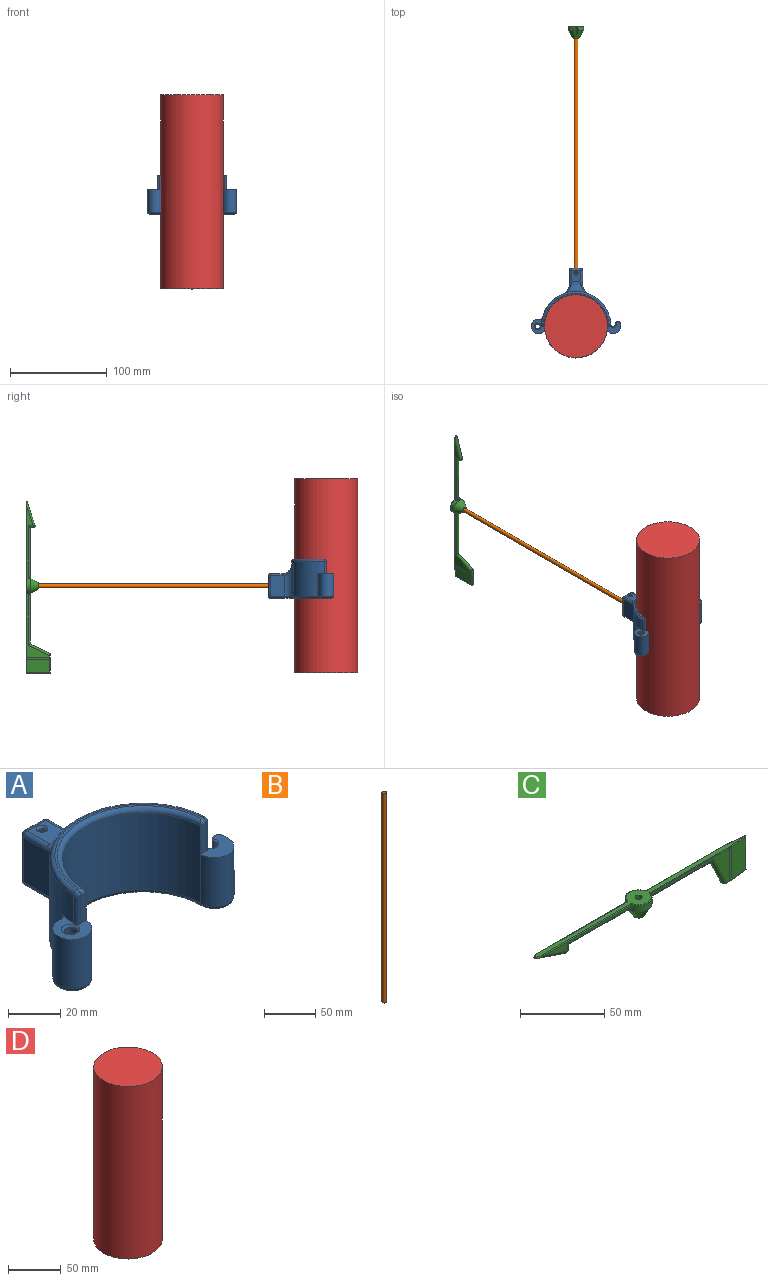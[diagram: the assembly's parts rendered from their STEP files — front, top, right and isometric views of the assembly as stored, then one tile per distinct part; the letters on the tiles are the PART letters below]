
ASSEMBLY  parts=4 mates=3
PART A: 71 faces, bbox 93.2x68.2x42.1 mm
  f0: cylinder r=2mm len=19mm, axis (0,1,0), area 228.4mm2, adj f22,f26,f27,f68
  f1: plane 13x2.94mm, normal (0,-1,0), area 38.2mm2, adj f4,f16,f63,f66
  f2: cylinder r=36mm len=71.88mm, axis (0,0,-1), area 2847.7mm2, adj f7,f17,f20,f23,f24,f25,f36,f39
  f3: plane 13x2.94mm, normal (0,-1,0), area 38.2mm2, adj f4,f7,f59,f60
  f4: cylinder r=31mm len=62mm, axis (0,0,-1), area 3506mm2, adj f1,f3,f8,f9,f33,f61
  f5: plane 67.88x32mm, normal (0,0,1), area 101.2mm2, adj f59,f61,f63,f64
  f6: plane 12.27x10mm, normal (0,0,1), area 105mm2, adj f24,f49,f53,f55,f67
  f7: plane 16.77x15mm, normal (0,0,1), area 116.2mm2, adj f2,f3,f9,f20,f60,f69
  f8: cylinder r=7.5mm len=23mm, axis (0,0,1), area 541.9mm2, adj f4,f14,f16,f31
  f9: cylinder r=7.5mm len=23mm, axis (0,0,1), area 835.4mm2, adj f4,f7,f20,f35
  f10: plane 21.38x15.26mm, normal (-1,0,0), area 320.8mm2, adj f25,f46,f52,f55,f56
  f11: plane 21x10mm, normal (0,1,0), area 181.7mm2, adj f47,f48,f52,f53,f68
  f12: plane 21.38x15.26mm, normal (1,0,0), area 320.8mm2, adj f23,f40,f45,f48,f49
  f13: plane 22.05x0.08mm, normal (0,1,0), area 1.8mm2, adj f17,f19,f32,f70
  f14: plane 23x2.5mm, normal (1,0,0), area 57.5mm2, adj f8,f16,f18,f29
  f15: plane 88x63.5mm, normal (0,0,-1), area 418.6mm2, adj f28,f29,f30,f31,f32,f33,f34,f35
  f16: plane 15x12.5mm, normal (0,0,1), area 105mm2, adj f1,f8,f14,f18,f66,f70
  f17: cylinder r=2.5mm len=22.39mm, axis (0,0,-1), area 84mm2, adj f2,f13,f34,f70
  f18: cylinder r=2.5mm len=23mm, axis (0,0,1), area 180mm2, adj f14,f16,f19,f28,f70
  f19: cylinder r=2.5mm len=22mm, axis (0,0,-1), area 86.4mm2, adj f13,f18,f30,f70
  f20: cylinder r=2.5mm len=23mm, axis (0,0,-1), area 82.8mm2, adj f2,f7,f9,f37
  f21: cylinder r=2.5mm len=22mm, axis (0,0,1), area 345.6mm2, adj f58,f69
  f22: cone r=0mm half-angle=59deg, axis (0,1,0), area 14.7mm2, adj f0
  f23: cylinder r=10mm len=33mm, axis (0,0,-1), area 310.3mm2, adj f2,f12,f38,f41
  f24: torus R=46mm, axis (0,0,-1), area 240.9mm2, adj f2,f6,f41,f45,f56,f57
  f25: cylinder r=10mm len=33mm, axis (0,0,-1), area 310.3mm2, adj f2,f10,f42,f57
  f26: cylinder r=1.25mm len=8.94mm, axis (0,0,1), area 68.4mm2, adj f0,f43
  f27: cylinder r=1.25mm len=9.94mm, axis (0,0,1), area 76.3mm2, adj f0,f67
  f28: torus R=0.5mm, axis (0,0,-1), area 17.5mm2, adj f15,f18,f29,f30
  f29: cylinder r=2mm len=2.5mm, axis (0,1,0), area 7.9mm2, adj f14,f15,f28,f31
  f30: torus R=4.5mm, axis (0,0,-1), area 15.9mm2, adj f15,f19,f28,f32
  f31: torus R=5.5mm, axis (0,0,-1), area 66.8mm2, adj f8,f15,f29,f33
  f32: cylinder r=2mm len=2mm, axis (-1,0,0), area 0.3mm2, adj f13,f15,f30,f34
  f33: torus R=33mm, axis (0,0,-1), area 313.1mm2, adj f4,f15,f31,f35
  f34: torus R=4.5mm, axis (0,0,-1), area 15.3mm2, adj f15,f17,f32,f36
  f35: torus R=5.5mm, axis (0,0,-1), area 103mm2, adj f9,f15,f33,f37
  f36: torus R=34mm, axis (0,0,-1), area 124.9mm2, adj f2,f15,f34,f38
  f37: torus R=4.5mm, axis (0,0,-1), area 14.6mm2, adj f15,f20,f35,f39
  f38: torus R=12mm, axis (0,0,-1), area 40.2mm2, adj f15,f23,f36,f40
  f39: torus R=34mm, axis (0,0,-1), area 103.3mm2, adj f2,f15,f37,f42
  f40: cylinder r=2mm len=15.26mm, axis (0,1,0), area 47.9mm2, adj f12,f15,f38,f44
  f41: bspline ~11.97x11.41mm, area 27.7mm2, adj f23,f24,f45
  f42: torus R=12mm, axis (0,0,-1), area 40.2mm2, adj f15,f25,f39,f46
  f43: torus R=3.25mm, axis (0,0,-1), area 38.8mm2, adj f15,f26,f47
  f44: sphere r=2mm, area 6.3mm2, adj f40,f47,f48
  f45: bspline ~5.65x2.65mm, area 8.4mm2, adj f12,f24,f41,f49
  f46: cylinder r=2mm len=15.26mm, axis (0,-1,0), area 47.9mm2, adj f10,f15,f42,f50
  f47: cylinder r=2mm len=10mm, axis (-1,0,0), area 31.2mm2, adj f11,f15,f43,f44,f50
  f48: cylinder r=2mm len=21mm, axis (0,0,1), area 66mm2, adj f11,f12,f44,f51
  f49: cylinder r=2mm len=12.27mm, axis (0,-1,0), area 38.6mm2, adj f6,f12,f45,f51
  f50: sphere r=2mm, area 6.3mm2, adj f46,f47,f52
  f51: sphere r=2mm, area 6.3mm2, adj f48,f49,f53
  f52: cylinder r=2mm len=21mm, axis (0,0,1), area 66mm2, adj f10,f11,f50,f54
  f53: cylinder r=2mm len=10mm, axis (1,0,0), area 31.4mm2, adj f6,f11,f51,f54
  f54: sphere r=2mm, area 6.3mm2, adj f52,f53,f55
  f55: cylinder r=2mm len=12.27mm, axis (0,1,0), area 38.6mm2, adj f6,f10,f54,f56
  f56: bspline ~5.65x2.65mm, area 8.4mm2, adj f10,f24,f55,f57
  f57: bspline ~11.97x11.41mm, area 27.7mm2, adj f24,f25,f56
  f58: torus R=4.5mm, axis (0,0,-1), area 63.7mm2, adj f15,f21
  f59: cylinder r=2mm len=2.94mm, axis (-1,0,0), area 7mm2, adj f3,f5,f61,f62
  f60: cylinder r=2mm len=13mm, axis (0,0,-1), area 42.4mm2, adj f2,f3,f7,f62
  f61: torus R=33mm, axis (0,0,1), area 308.6mm2, adj f4,f5,f59,f63
  f62: sphere r=2mm, area 6.5mm2, adj f59,f60,f64
  f63: cylinder r=2mm len=2.94mm, axis (-1,0,0), area 7mm2, adj f1,f5,f61,f65
  f64: torus R=34mm, axis (0,0,1), area 335.1mm2, adj f2,f5,f62,f65
  f65: sphere r=2mm, area 6.5mm2, adj f63,f64,f66
  f66: cylinder r=2mm len=13.58mm, axis (0,0,-1), area 42.7mm2, adj f1,f2,f16,f65,f70
  f67: torus R=2.25mm, axis (0,0,-1), area 15.9mm2, adj f6,f27
  f68: torus R=3mm, axis (0,-1,0), area 23.3mm2, adj f0,f11
  f69: torus R=3.5mm, axis (0,0,-1), area 28.3mm2, adj f7,f21
  f70: torus R=3.5mm, axis (0,0,-1), area 12.9mm2, adj f2,f13,f16,f17,f18,f19,f66
PART B: 3 faces, bbox 4x4x250 mm
  f0: cylinder r=2mm len=250mm, axis (0,0,-1), area 3141.6mm2, adj f1,f2
  f1: plane 4x4mm, normal (0,0,1), area 12.6mm2, adj f0
  f2: plane 4x4mm, normal (0,0,-1), area 12.6mm2, adj f0
PART C: 56 faces, bbox 177.5x17.3x26.3 mm
  f0: plane 65.88x24mm, normal (0,-1,0), area 264.9mm2, adj f3,f11,f12,f18,f26,f49
  f1: plane 65.88x24mm, normal (0,1,0), area 264.9mm2, adj f11,f12,f19,f25,f36,f53
  f2: cylinder r=2mm len=53.88mm, axis (-1,0,0), area 327.3mm2, adj f8,f9,f39,f46
  f3: cylinder r=0.5mm len=65.88mm, axis (1,0,0), area 51.7mm2, adj f0,f5,f24,f47
  f4: cylinder r=0.5mm len=74.05mm, axis (-1,0,0), area 58.2mm2, adj f5,f9,f22,f50
  f5: plane 176.89x15mm, normal (0,0,1), area 623.7mm2, adj f3,f4,f21,f22,f24,f25,f27,f28
  f6: plane 18.71x3mm, normal (0,0,-1), area 33.5mm2, adj f10,f23,f26,f29,f32,f34,f35,f36
  f7: plane 25x0.1mm, normal (1,0,0), area 2.4mm2, adj f27,f30,f31,f32,f33,f34
  f8: plane 74.05x6.73mm, normal (0,-1,0), area 148.7mm2, adj f2,f13,f14,f21,f44
  f9: plane 74.05x6.73mm, normal (0,1,0), area 148.7mm2, adj f2,f4,f13,f14,f48
  f10: cylinder r=2mm len=2.71mm, axis (0,1,0), area 3.4mm2, adj f6,f20,f38
  f11: cylinder r=2mm len=23.36mm, axis (-0.43,0,0.9), area 147.2mm2, adj f0,f1,f12,f20,f23,f37,f38
  f12: cylinder r=2mm len=53.14mm, axis (-1,0,0), area 327.6mm2, adj f0,f1,f11,f51
  f13: cylinder r=2mm len=25.09mm, axis (-0.95,0,0.32), area 151.6mm2, adj f8,f9,f15,f22
  f14: cylinder r=2mm len=5.23mm, axis (0,0,-1), area 22.8mm2, adj f8,f9,f15,f39
  f15: sphere r=2mm, area 15.1mm2, adj f13,f14
  f16: plane 24x13.56mm, normal (0.1,1,0), area 327mm2, adj f19,f31,f33,f34
  f17: plane 24x13.56mm, normal (0.1,-1,0), area 327mm2, adj f18,f27,f30,f32
  f18: cylinder r=20mm len=24mm, axis (0,0,-1), area 47.8mm2, adj f0,f17,f24,f29
  f19: cylinder r=20mm len=24mm, axis (0,0,1), area 47.8mm2, adj f1,f16,f28,f35
  f20: bspline ~1.97x1.87mm, area 1mm2, adj f10,f11,f23
  f21: cylinder r=0.5mm len=74.05mm, axis (1,0,0), area 58.2mm2, adj f5,f8,f22,f43
  f22: bspline ~5.23x4mm, area 12.7mm2, adj f4,f5,f13,f21
  f23: bspline ~1.51x0.75mm, area 0.6mm2, adj f6,f11,f20,f26
  f24: torus R=19.5mm, axis (0,0,1), area 1.6mm2, adj f3,f5,f18,f27
  f25: cylinder r=0.5mm len=65.88mm, axis (-1,0,0), area 51.7mm2, adj f1,f5,f28,f54
  f26: cylinder r=0.5mm len=2.03mm, axis (-1,0,0), area 1.6mm2, adj f0,f6,f23,f29
  f27: cylinder r=0.5mm len=14.11mm, axis (-1,-0.1,0), area 11mm2, adj f5,f7,f17,f24,f30,f31
  f28: torus R=19.5mm, axis (0,0,1), area 1.6mm2, adj f5,f19,f25,f31
  f29: torus R=19.5mm, axis (0,0,-1), area 1.6mm2, adj f6,f18,f26,f32
  f30: cylinder r=0.5mm len=25mm, axis (0,0,1), area 18.1mm2, adj f7,f17,f27,f32
  f31: cylinder r=0.5mm len=14.11mm, axis (-1,0.1,0), area 11mm2, adj f5,f7,f16,f27,f28,f33
  f32: cylinder r=0.5mm len=14.11mm, axis (1,0.1,0), area 11mm2, adj f6,f7,f17,f29,f30,f34
  f33: cylinder r=0.5mm len=25mm, axis (0,0,1), area 18.1mm2, adj f7,f16,f31,f34
  f34: cylinder r=0.5mm len=14.11mm, axis (1,-0.1,0), area 11mm2, adj f6,f7,f16,f32,f33,f35
  f35: torus R=19.5mm, axis (0,0,-1), area 1.6mm2, adj f6,f19,f34,f36
  f36: cylinder r=0.5mm len=2.03mm, axis (1,0,0), area 1.6mm2, adj f1,f6,f35,f37
  f37: bspline ~1.51x0.75mm, area 0.6mm2, adj f6,f11,f36,f38
  f38: bspline ~1.97x1.87mm, area 1mm2, adj f10,f11,f37
  f39: bspline ~4x2.5mm, area 3.5mm2, adj f2,f14
  f40: cylinder r=8mm len=16mm, axis (0,0,1), area 193.2mm2, adj f41,f44,f45,f46,f48,f49,f51,f52
  f41: cone r=8mm half-angle=31.8deg, axis (0,0,1), area 326.5mm2, adj f40,f42
  f42: plane 6.08x6.08mm, normal (0,0,-1), area 15.2mm2, adj f41,f55
  f43: torus R=1mm, axis (0,0,1), area 0.7mm2, adj f5,f21,f44,f45
  f44: cylinder r=0.5mm len=1.5mm, axis (0,0,1), area 1mm2, adj f8,f40,f43,f46
  f45: torus R=7.5mm, axis (0,0,1), area 15.6mm2, adj f5,f40,f43,f47
  f46: bspline ~4.71x3.05mm, area 4.8mm2, adj f2,f40,f44,f48
  f47: torus R=1mm, axis (0,0,1), area 0.7mm2, adj f3,f5,f45,f49
  f48: cylinder r=0.5mm len=1.5mm, axis (0,0,1), area 1mm2, adj f9,f40,f46,f50
  f49: cylinder r=0.5mm len=1.5mm, axis (0,0,1), area 1mm2, adj f0,f40,f47,f51
  f50: torus R=1mm, axis (0,0,1), area 0.7mm2, adj f4,f5,f48,f52
  f51: bspline ~4.71x3.05mm, area 4.8mm2, adj f12,f40,f49,f53
  f52: torus R=7.5mm, axis (0,0,1), area 15.6mm2, adj f5,f40,f50,f54
  f53: cylinder r=0.5mm len=1.5mm, axis (0,0,1), area 1mm2, adj f1,f40,f51,f54
  f54: torus R=1mm, axis (0,0,1), area 0.7mm2, adj f5,f25,f52,f53
  f55: cylinder r=2.1mm len=13mm, axis (0,0,1), area 171.5mm2, adj f5,f42
PART D: 3 faces, bbox 65x65x200 mm
  f0: cylinder r=32.5mm len=200mm, axis (0,0,1), area 40840.7mm2, adj f1,f2
  f1: plane 65x65mm, normal (0,0,-1), area 3318.3mm2, adj f0
  f2: plane 65x65mm, normal (0,0,1), area 3318.3mm2, adj f0
PLACE A rot(axis=(-0.3,0.89,0.34),0deg) t=(-61.59,-41.06,29.52)mm
PLACE B rot(axis=(1,0,0),90deg) t=(-61.59,268.94,17.02)mm
PLACE C rot(axis=(-0.58,0.58,0.58),120deg) t=(-61.59,268.94,17.02)mm
PLACE D rot(axis=(-0.3,0.89,0.34),0deg) t=(-61.59,-41.06,27.52)mm
MATE fastened B.f0 <-> A.f0  axis (0,1,0) through (-61.59,18.94,17.02)mm
MATE revolute C.f40 <-> B.f0  axis (0,1,0) through (-61.59,268.94,17.02)mm
MATE slider A.f4 <-> D.f0  axis (0,0,-1) through (-61.59,-41.06,42.52)mm
